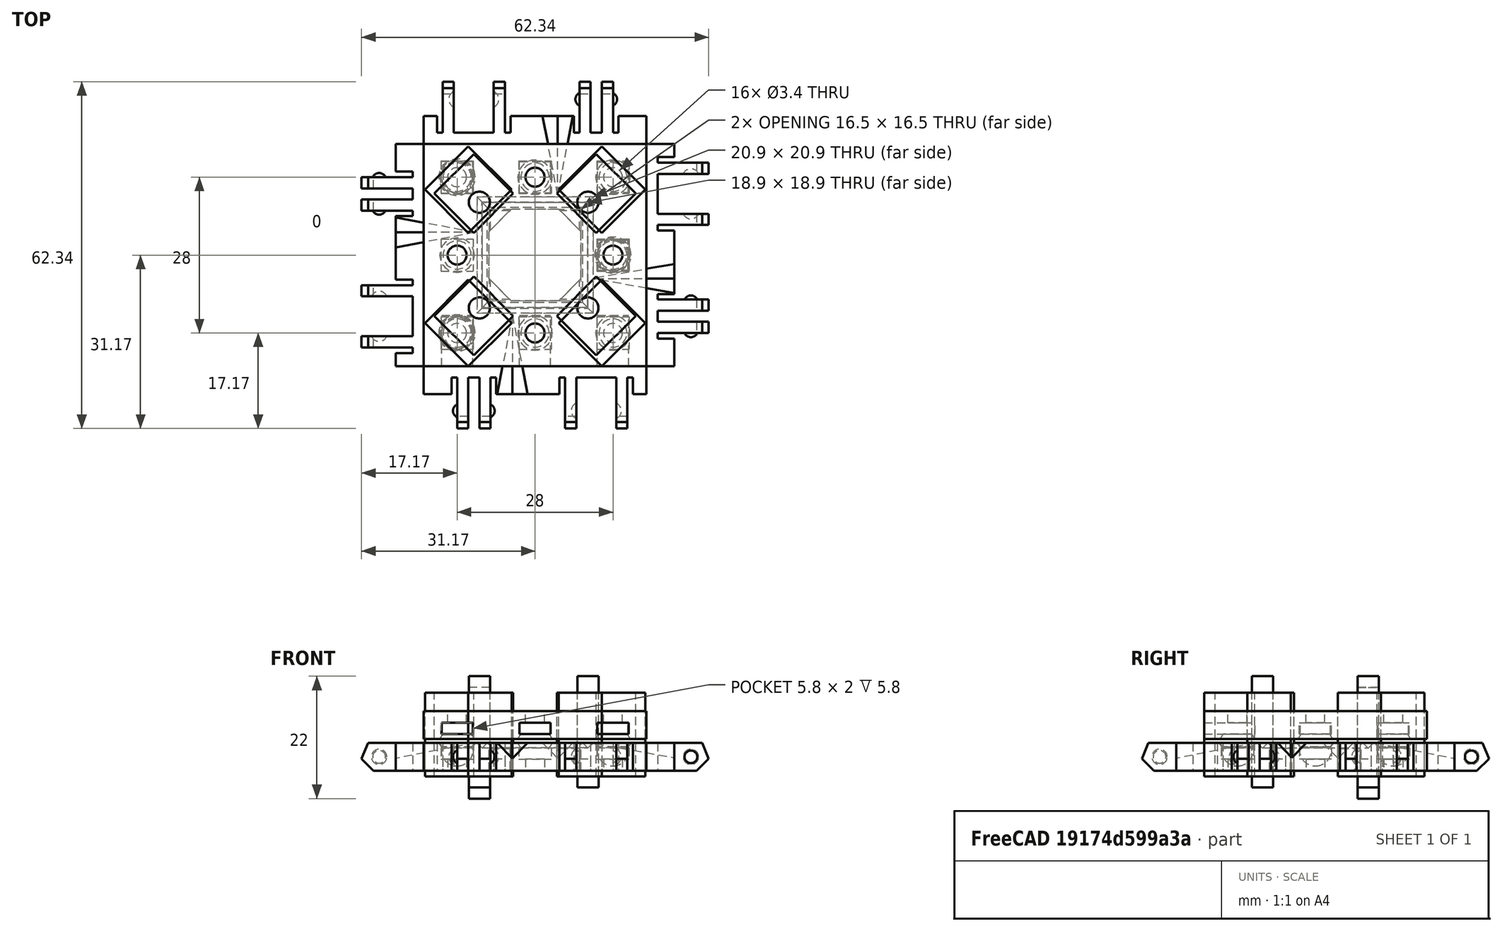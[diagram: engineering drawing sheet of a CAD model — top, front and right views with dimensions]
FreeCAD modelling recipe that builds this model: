
FCSTD DOCUMENT  (FreeCAD 0.17R13522 (Git))
Label: Robot Plates 0.1
License: All rights reserved
LicenseURL: http://en.wikipedia.org/wiki/All_rights_reserved
objects: Part::Box×147, Part::Sphere×51, Part::MultiFuse×48, Part::Cut×47, Part::Cylinder×24, Part::Chamfer×13, Part::Fuse×2, App::DocumentObjectGroup×1
note: 332 computed .brp shape members not serialized (recipe doc carries the construction recipe); baked Part::Feature solids carry a one-line shape summary decoded from their .brp

FEATURE [Part::Box] Box  label="Cube"
  AttacherType = Attacher::AttachEngine3D
  Height = 5
  Length = 40
  Placement = pos=(0,0,-2) rot=(0,0,1;0rad)
  Width = 40
FEATURE [Part::Sphere] Sphere003  label="Mag Hole 3"
  Angle1 = -90
  Angle2 = 90
  Angle3 = 360
  AttacherType = Attacher::AttachEngine3D
  Placement = pos=(6,34,1.7) rot=(0,0,1;0rad)
  Radius = 2.85
FEATURE [Part::Sphere] Sphere005  label="Mag Hole 2"
  Angle1 = -90
  Angle2 = 90
  Angle3 = 360
  AttacherType = Attacher::AttachEngine3D
  Placement = pos=(34,20,1.7) rot=(0,0,1;0rad)
  Radius = 2.85
FEATURE [Part::Sphere] Sphere  label="Mag Hole"
  Angle1 = -90
  Angle2 = 90
  Angle3 = 360
  AttacherType = Attacher::AttachEngine3D
  Placement = pos=(6,6,1.7) rot=(0,0,1;0rad)
  Radius = 2.85
FEATURE [Part::MultiFuse] Fusion004
  Shapes = -> [Sphere,Sphere005,Sphere003]
FEATURE [Part::Cut] Cut003
  Base = -> Box
  Tool = -> Fusion004
FEATURE [Part::Chamfer] Chamfer
  Base = -> Cut003
  Edges = 3 edges r=0.75: [Edge10,Edge11,Edge12]
FEATURE [Part::Box] Box001  label="Cube001"
  AttacherType = Attacher::AttachEngine3D
  Height = 7
  Length = 5
  Width = 40
FEATURE [Part::Box] Box002  label="Cube002"
  AttacherType = Attacher::AttachEngine3D
  Height = 7
  Length = 10
  Placement = pos=(-10,6,0) rot=(0,0,1;0rad)
  Width = 2
FEATURE [Part::Box] Box003  label="Cube003"
  AttacherType = Attacher::AttachEngine3D
  Height = 7
  Length = 10
  Placement = pos=(-10,10,0) rot=(0,0,1;0rad)
  Width = 2
FEATURE [Part::Box] Box004  label="Cube004"
  AttacherType = Attacher::AttachEngine3D
  Height = 7
  Length = 10
  Placement = pos=(-10,25.4,0) rot=(0,0,1;0rad)
  Width = 2
FEATURE [Part::Box] Box005  label="Cube005"
  AttacherType = Attacher::AttachEngine3D
  Height = 7
  Length = 10
  Placement = pos=(-10,34.6,0) rot=(0,0,1;0rad)
  Width = 2
FEATURE [Part::Sphere] Sphere008
  Angle1 = -90
  Angle2 = 90
  Angle3 = 360
  AttacherType = Attacher::AttachEngine3D
  Placement = pos=(-3,6.5,2.5) rot=(0,0,1;0rad)
  Radius = 1.25
FEATURE [Part::Box] Box006  label="Cube006"
  AttacherType = Attacher::AttachEngine3D
  Height = 10
  Length = 13
  Placement = pos=(-10.19,0,-1.19) rot=(0,-1,0;0.785398rad)
  Width = 40
FEATURE [Part::Sphere] Sphere009
  Angle1 = -90
  Angle2 = 90
  Angle3 = 360
  AttacherType = Attacher::AttachEngine3D
  Placement = pos=(-3,11.5,2.5) rot=(0,0,1;0rad)
  Radius = 1.25
FEATURE [Part::Sphere] Sphere010
  Angle1 = -90
  Angle2 = 90
  Angle3 = 360
  AttacherType = Attacher::AttachEngine3D
  Placement = pos=(-3,28,2.5) rot=(0,0,1;0rad)
  Radius = 1.5
FEATURE [Part::Sphere] Sphere011
  Angle1 = -90
  Angle2 = 90
  Angle3 = 360
  AttacherType = Attacher::AttachEngine3D
  Placement = pos=(-3,34,2.5) rot=(0,0,1;0rad)
  Radius = 1.5
FEATURE [Part::MultiFuse] Fusion
  Shapes = -> [Box001,Box002,Box003,Box004,Box005]
FEATURE [Part::Cut] Cut
  Base = -> Fusion
  Tool = -> Box006
FEATURE [Part::MultiFuse] Fusion001
  Shapes = -> [Sphere008,Sphere009,Cut]
FEATURE [Part::MultiFuse] Fusion002
  Shapes = -> [Sphere011,Sphere010]
FEATURE [Part::Cut] Cut001
  Base = -> Fusion001
  Tool = -> Fusion002
FEATURE [Part::Chamfer] Chamfer001
  Base = -> Cut001
  Edges = 4 edges r=4: [Edge31,Edge37,Edge43,Edge46]
FEATURE [Part::Box] Box007  label="Cube007"
  AttacherType = Attacher::AttachEngine3D
  Height = 7
  Length = 4
  Placement = pos=(-1,5,0) rot=(0,0,1;0rad)
  Width = 1
FEATURE [Part::Box] Box008  label="Cube008"
  AttacherType = Attacher::AttachEngine3D
  Height = 7
  Length = 4
  Placement = pos=(-1,8,0) rot=(0,0,1;0rad)
  Width = 2
FEATURE [Part::Box] Box009  label="Cube009"
  AttacherType = Attacher::AttachEngine3D
  Height = 7
  Length = 4
  Placement = pos=(-1,12,0) rot=(0,0,1;0rad)
  Width = 1
FEATURE [Part::Box] Box010  label="Cube010"
  AttacherType = Attacher::AttachEngine3D
  Height = 7
  Length = 4
  Placement = pos=(-1,24.4,0) rot=(0,0,1;0rad)
  Width = 1
FEATURE [Part::Box] Box011  label="Cube011"
  AttacherType = Attacher::AttachEngine3D
  Height = 7
  Length = 4
  Placement = pos=(-1,36.6,0) rot=(0,0,1;0rad)
  Width = 1
FEATURE [Part::Box] Box012  label="Cube012"
  AttacherType = Attacher::AttachEngine3D
  Height = 7
  Length = 4
  Placement = pos=(-1,27.4,0) rot=(0,0,1;0rad)
  Width = 7.2
FEATURE [Part::MultiFuse] Fusion003
  Shapes = -> [Box012,Box009,Box011,Box008,Box010,Box007]
FEATURE [Part::Cut] Cut002
  Base = -> Chamfer001
  Placement = pos=(-5,40,3) rot=(1,0,0;3.14159rad)
  Tool = -> Fusion003
FEATURE [Part::Box] Box013  label="Cube013"
  AttacherType = Attacher::AttachEngine3D
  Height = 10
  Length = 12
  Placement = pos=(-11,-2,-12) rot=(0,0,1;0rad)
  Width = 44
FEATURE [Part::Cut] Cut004
  Base = -> Cut002
  Tool = -> Box013
FEATURE [Part::Box] Box014  label="Cube014"
  AttacherType = Attacher::AttachEngine3D
  Height = 7
  Length = 10
  Placement = pos=(-10,34.6,0) rot=(0,0,1;0rad)
  Width = 2
FEATURE [Part::Box] Box015  label="Cube015"
  AttacherType = Attacher::AttachEngine3D
  Height = 7
  Length = 5
  Width = 40
FEATURE [Part::Box] Box016  label="Cube016"
  AttacherType = Attacher::AttachEngine3D
  Height = 7
  Length = 10
  Placement = pos=(-10,25.4,0) rot=(0,0,1;0rad)
  Width = 2
FEATURE [Part::Box] Box017  label="Cube017"
  AttacherType = Attacher::AttachEngine3D
  Height = 7
  Length = 10
  Placement = pos=(-10,10,0) rot=(0,0,1;0rad)
  Width = 2
FEATURE [Part::Box] Box018  label="Cube018"
  AttacherType = Attacher::AttachEngine3D
  Height = 7
  Length = 10
  Placement = pos=(-10,6,0) rot=(0,0,1;0rad)
  Width = 2
FEATURE [Part::Sphere] Sphere012
  Angle1 = -90
  Angle2 = 90
  Angle3 = 360
  AttacherType = Attacher::AttachEngine3D
  Placement = pos=(-3,6.5,2.5) rot=(0,0,1;0rad)
  Radius = 1.25
FEATURE [Part::Box] Box019  label="Cube019"
  AttacherType = Attacher::AttachEngine3D
  Height = 10
  Length = 13
  Placement = pos=(-10.19,0,-1.19) rot=(0,-1,0;0.785398rad)
  Width = 40
FEATURE [Part::Sphere] Sphere013
  Angle1 = -90
  Angle2 = 90
  Angle3 = 360
  AttacherType = Attacher::AttachEngine3D
  Placement = pos=(-3,11.5,2.5) rot=(0,0,1;0rad)
  Radius = 1.25
FEATURE [Part::Sphere] Sphere014
  Angle1 = -90
  Angle2 = 90
  Angle3 = 360
  AttacherType = Attacher::AttachEngine3D
  Placement = pos=(-3,28,2.5) rot=(0,0,1;0rad)
  Radius = 1.5
FEATURE [Part::Sphere] Sphere015
  Angle1 = -90
  Angle2 = 90
  Angle3 = 360
  AttacherType = Attacher::AttachEngine3D
  Placement = pos=(-3,34,2.5) rot=(0,0,1;0rad)
  Radius = 1.5
FEATURE [Part::MultiFuse] Fusion005
  Shapes = -> [Box015,Box018,Box017,Box016,Box014]
FEATURE [Part::Cut] Cut005
  Base = -> Fusion005
  Tool = -> Box019
FEATURE [Part::MultiFuse] Fusion006
  Shapes = -> [Sphere012,Sphere013,Cut005]
FEATURE [Part::MultiFuse] Fusion007
  Shapes = -> [Sphere015,Sphere014]
FEATURE [Part::Cut] Cut006
  Base = -> Fusion006
  Tool = -> Fusion007
FEATURE [Part::Chamfer] Chamfer002
  Base = -> Cut006
  Edges = 4 edges r=4: [Edge31,Edge37,Edge43,Edge46]
FEATURE [Part::Box] Box020  label="Cube020"
  AttacherType = Attacher::AttachEngine3D
  Height = 7
  Length = 4
  Placement = pos=(-1,5,0) rot=(0,0,1;0rad)
  Width = 1
FEATURE [Part::Box] Box021  label="Cube021"
  AttacherType = Attacher::AttachEngine3D
  Height = 7
  Length = 4
  Placement = pos=(-1,8,0) rot=(0,0,1;0rad)
  Width = 2
FEATURE [Part::Box] Box022  label="Cube022"
  AttacherType = Attacher::AttachEngine3D
  Height = 7
  Length = 4
  Placement = pos=(-1,12,0) rot=(0,0,1;0rad)
  Width = 1
FEATURE [Part::Box] Box023  label="Cube023"
  AttacherType = Attacher::AttachEngine3D
  Height = 7
  Length = 4
  Placement = pos=(-1,24.4,0) rot=(0,0,1;0rad)
  Width = 1
FEATURE [Part::Box] Box024  label="Cube024"
  AttacherType = Attacher::AttachEngine3D
  Height = 7
  Length = 4
  Placement = pos=(-1,36.6,0) rot=(0,0,1;0rad)
  Width = 1
FEATURE [Part::Box] Box025  label="Cube025"
  AttacherType = Attacher::AttachEngine3D
  Height = 7
  Length = 4
  Placement = pos=(-1,27.4,0) rot=(0,0,1;0rad)
  Width = 7.2
FEATURE [Part::MultiFuse] Fusion008
  Shapes = -> [Box025,Box022,Box024,Box021,Box023,Box020]
FEATURE [Part::Cut] Cut007
  Base = -> Chamfer002
  Placement = pos=(-5,40,3) rot=(1,0,0;3.14159rad)
  Tool = -> Fusion008
FEATURE [Part::Box] Box026  label="Cube026"
  AttacherType = Attacher::AttachEngine3D
  Height = 10
  Length = 12
  Placement = pos=(-11,-2,-12) rot=(0,0,1;0rad)
  Width = 44
FEATURE [Part::Cut] Cut008
  Base = -> Cut007
  Placement = pos=(40,0,0) rot=(0,0,1;1.5708rad)
  Tool = -> Box026
FEATURE [Part::Box] Box027  label="Cube027"
  AttacherType = Attacher::AttachEngine3D
  Height = 7
  Length = 4
  Placement = pos=(-1,12,0) rot=(0,0,1;0rad)
  Width = 1
FEATURE [Part::Box] Box028  label="Cube028"
  AttacherType = Attacher::AttachEngine3D
  Height = 10
  Length = 13
  Placement = pos=(-10.19,0,-1.19) rot=(0,-1,0;0.785398rad)
  Width = 40
FEATURE [Part::Box] Box029  label="Cube029"
  AttacherType = Attacher::AttachEngine3D
  Height = 7
  Length = 4
  Placement = pos=(-1,27.4,0) rot=(0,0,1;0rad)
  Width = 7.2
FEATURE [Part::Box] Box030  label="Cube030"
  AttacherType = Attacher::AttachEngine3D
  Height = 7
  Length = 4
  Placement = pos=(-1,5,0) rot=(0,0,1;0rad)
  Width = 1
FEATURE [Part::Box] Box031  label="Cube031"
  AttacherType = Attacher::AttachEngine3D
  Height = 7
  Length = 10
  Placement = pos=(-10,6,0) rot=(0,0,1;0rad)
  Width = 2
FEATURE [Part::Box] Box032  label="Cube032"
  AttacherType = Attacher::AttachEngine3D
  Height = 10
  Length = 12
  Placement = pos=(-11,-2,-12) rot=(0,0,1;0rad)
  Width = 44
FEATURE [Part::Sphere] Sphere016
  Angle1 = -90
  Angle2 = 90
  Angle3 = 360
  AttacherType = Attacher::AttachEngine3D
  Placement = pos=(-3,6.5,2.5) rot=(0,0,1;0rad)
  Radius = 1.25
FEATURE [Part::Box] Box033  label="Cube033"
  AttacherType = Attacher::AttachEngine3D
  Height = 7
  Length = 10
  Placement = pos=(-10,25.4,0) rot=(0,0,1;0rad)
  Width = 2
FEATURE [Part::Box] Box034  label="Cube034"
  AttacherType = Attacher::AttachEngine3D
  Height = 7
  Length = 10
  Placement = pos=(-10,10,0) rot=(0,0,1;0rad)
  Width = 2
FEATURE [Part::Sphere] Sphere017
  Angle1 = -90
  Angle2 = 90
  Angle3 = 360
  AttacherType = Attacher::AttachEngine3D
  Placement = pos=(-3,28,2.5) rot=(0,0,1;0rad)
  Radius = 1.5
FEATURE [Part::Sphere] Sphere018
  Angle1 = -90
  Angle2 = 90
  Angle3 = 360
  AttacherType = Attacher::AttachEngine3D
  Placement = pos=(-3,11.5,2.5) rot=(0,0,1;0rad)
  Radius = 1.25
FEATURE [Part::Box] Box035  label="Cube035"
  AttacherType = Attacher::AttachEngine3D
  Height = 7
  Length = 4
  Placement = pos=(-1,36.6,0) rot=(0,0,1;0rad)
  Width = 1
FEATURE [Part::Sphere] Sphere019
  Angle1 = -90
  Angle2 = 90
  Angle3 = 360
  AttacherType = Attacher::AttachEngine3D
  Placement = pos=(-3,34,2.5) rot=(0,0,1;0rad)
  Radius = 1.5
FEATURE [Part::MultiFuse] Fusion011
  Shapes = -> [Sphere019,Sphere017]
FEATURE [Part::Box] Box036  label="Cube036"
  AttacherType = Attacher::AttachEngine3D
  Height = 7
  Length = 4
  Placement = pos=(-1,8,0) rot=(0,0,1;0rad)
  Width = 2
FEATURE [Part::Box] Box037  label="Cube037"
  AttacherType = Attacher::AttachEngine3D
  Height = 7
  Length = 10
  Placement = pos=(-10,34.6,0) rot=(0,0,1;0rad)
  Width = 2
FEATURE [Part::Box] Box038  label="Cube038"
  AttacherType = Attacher::AttachEngine3D
  Height = 7
  Length = 4
  Placement = pos=(-1,24.4,0) rot=(0,0,1;0rad)
  Width = 1
FEATURE [Part::MultiFuse] Fusion009
  Shapes = -> [Box029,Box027,Box035,Box036,Box038,Box030]
FEATURE [Part::Box] Box039  label="Cube039"
  AttacherType = Attacher::AttachEngine3D
  Height = 7
  Length = 5
  Width = 40
FEATURE [Part::MultiFuse] Fusion012
  Shapes = -> [Box039,Box031,Box034,Box033,Box037]
FEATURE [Part::Cut] Cut011
  Base = -> Fusion012
  Tool = -> Box028
FEATURE [Part::MultiFuse] Fusion010
  Shapes = -> [Sphere016,Sphere018,Cut011]
FEATURE [Part::Cut] Cut012
  Base = -> Fusion010
  Tool = -> Fusion011
FEATURE [Part::Chamfer] Chamfer003
  Base = -> Cut012
  Edges = 4 edges r=4: [Edge31,Edge37,Edge43,Edge46]
FEATURE [Part::Cut] Cut010
  Base = -> Chamfer003
  Placement = pos=(-5,40,3) rot=(1,0,0;3.14159rad)
  Tool = -> Fusion009
FEATURE [Part::Cut] Cut009
  Base = -> Cut010
  Placement = pos=(40,40,0) rot=(0,0,1;3.14159rad)
  Tool = -> Box032
FEATURE [Part::Sphere] Sphere020
  Angle1 = -90
  Angle2 = 90
  Angle3 = 360
  AttacherType = Attacher::AttachEngine3D
  Placement = pos=(-3,11.5,2.5) rot=(0,0,1;0rad)
  Radius = 1.25
FEATURE [Part::Box] Box040  label="Cube040"
  AttacherType = Attacher::AttachEngine3D
  Height = 7
  Length = 10
  Placement = pos=(-10,6,0) rot=(0,0,1;0rad)
  Width = 2
FEATURE [Part::Box] Box041  label="Cube041"
  AttacherType = Attacher::AttachEngine3D
  Height = 7
  Length = 4
  Placement = pos=(-1,8,0) rot=(0,0,1;0rad)
  Width = 2
FEATURE [Part::Box] Box042  label="Cube042"
  AttacherType = Attacher::AttachEngine3D
  Height = 7
  Length = 10
  Placement = pos=(-10,10,0) rot=(0,0,1;0rad)
  Width = 2
FEATURE [Part::Box] Box043  label="Cube043"
  AttacherType = Attacher::AttachEngine3D
  Height = 10
  Length = 12
  Placement = pos=(-11,-2,-12) rot=(0,0,1;0rad)
  Width = 44
FEATURE [Part::Box] Box044  label="Cube044"
  AttacherType = Attacher::AttachEngine3D
  Height = 7
  Length = 4
  Placement = pos=(-1,5,0) rot=(0,0,1;0rad)
  Width = 1
FEATURE [Part::Sphere] Sphere021
  Angle1 = -90
  Angle2 = 90
  Angle3 = 360
  AttacherType = Attacher::AttachEngine3D
  Placement = pos=(-3,28,2.5) rot=(0,0,1;0rad)
  Radius = 1.5
FEATURE [Part::Sphere] Sphere022
  Angle1 = -90
  Angle2 = 90
  Angle3 = 360
  AttacherType = Attacher::AttachEngine3D
  Placement = pos=(-3,6.5,2.5) rot=(0,0,1;0rad)
  Radius = 1.25
FEATURE [Part::Sphere] Sphere023
  Angle1 = -90
  Angle2 = 90
  Angle3 = 360
  AttacherType = Attacher::AttachEngine3D
  Placement = pos=(-3,34,2.5) rot=(0,0,1;0rad)
  Radius = 1.5
FEATURE [Part::Box] Box045  label="Cube045"
  AttacherType = Attacher::AttachEngine3D
  Height = 7
  Length = 4
  Placement = pos=(-1,12,0) rot=(0,0,1;0rad)
  Width = 1
FEATURE [Part::Box] Box046  label="Cube046"
  AttacherType = Attacher::AttachEngine3D
  Height = 7
  Length = 5
  Width = 40
FEATURE [Part::Box] Box047  label="Cube047"
  AttacherType = Attacher::AttachEngine3D
  Height = 7
  Length = 4
  Placement = pos=(-1,36.6,0) rot=(0,0,1;0rad)
  Width = 1
FEATURE [Part::Box] Box048  label="Cube048"
  AttacherType = Attacher::AttachEngine3D
  Height = 7
  Length = 4
  Placement = pos=(-1,24.4,0) rot=(0,0,1;0rad)
  Width = 1
FEATURE [Part::Box] Box049  label="Cube049"
  AttacherType = Attacher::AttachEngine3D
  Height = 7
  Length = 10
  Placement = pos=(-10,25.4,0) rot=(0,0,1;0rad)
  Width = 2
FEATURE [Part::Box] Box050  label="Cube050"
  AttacherType = Attacher::AttachEngine3D
  Height = 10
  Length = 13
  Placement = pos=(-10.19,0,-1.19) rot=(0,-1,0;0.785398rad)
  Width = 40
FEATURE [Part::Box] Box051  label="Cube051"
  AttacherType = Attacher::AttachEngine3D
  Height = 7
  Length = 10
  Placement = pos=(-10,34.6,0) rot=(0,0,1;0rad)
  Width = 2
FEATURE [Part::MultiFuse] Fusion015
  Shapes = -> [Box046,Box040,Box042,Box049,Box051]
FEATURE [Part::Cut] Cut013
  Base = -> Fusion015
  Tool = -> Box050
FEATURE [Part::MultiFuse] Fusion013
  Shapes = -> [Sphere022,Sphere020,Cut013]
FEATURE [Part::MultiFuse] Fusion016
  Shapes = -> [Sphere023,Sphere021]
FEATURE [Part::Cut] Cut014
  Base = -> Fusion013
  Tool = -> Fusion016
FEATURE [Part::Chamfer] Chamfer004
  Base = -> Cut014
  Edges = 4 edges r=4: [Edge31,Edge37,Edge43,Edge46]
FEATURE [Part::Box] Box052  label="Cube052"
  AttacherType = Attacher::AttachEngine3D
  Height = 7
  Length = 4
  Placement = pos=(-1,27.4,0) rot=(0,0,1;0rad)
  Width = 7.2
FEATURE [Part::MultiFuse] Fusion014
  Shapes = -> [Box052,Box045,Box047,Box041,Box048,Box044]
FEATURE [Part::Cut] Cut016
  Base = -> Chamfer004
  Placement = pos=(-5,40,3) rot=(1,0,0;3.14159rad)
  Tool = -> Fusion014
FEATURE [Part::Cut] Cut015
  Base = -> Cut016
  Placement = pos=(0,40,0) rot=(0,0,-1;1.5708rad)
  Tool = -> Box043
FEATURE [Part::Box] Box054  label="Cube054"
  AttacherType = Attacher::AttachEngine3D
  Height = 15
  Length = 10
  Placement = pos=(9,2,-3) rot=(0,0,1;0.785398rad)
  Width = 10
FEATURE [Part::Box] Box055  label="Cube055"
  AttacherType = Attacher::AttachEngine3D
  Height = 15
  Length = 10
  Placement = pos=(31,24,-3) rot=(0,0,1;0.785398rad)
  Width = 10
FEATURE [Part::Box] Box056  label="Cube056"
  AttacherType = Attacher::AttachEngine3D
  Height = 15
  Length = 10
  Placement = pos=(31,2,-3) rot=(0,0,1;0.785398rad)
  Width = 10
FEATURE [Part::Box] Box057  label="Cube057"
  AttacherType = Attacher::AttachEngine3D
  Height = 15
  Length = 10
  Placement = pos=(9,24,-3) rot=(0,0,1;0.785398rad)
  Width = 10
FEATURE [Part::MultiFuse] Fusion017
  Shapes = -> [Box054,Box057,Box056,Box055]
FEATURE [Part::Box] Box058  label="Cube058"
  AttacherType = Attacher::AttachEngine3D
  Height = 5
  Length = 40
  Placement = pos=(0,0,3.7) rot=(0,0,1;0rad)
  Width = 40
FEATURE [Part::Box] Box059  label="Square Nut Hole 008"
  AttacherType = Attacher::AttachEngine3D
  Height = 2
  Length = 5.6
  Placement = pos=(17.2,31.2,4.6) rot=(0,0,1;0rad)
  Width = 5.6
FEATURE [Part::Box] Box060  label="Square Nut Hole 009"
  AttacherType = Attacher::AttachEngine3D
  Height = 2
  Length = 5.6
  Placement = pos=(17.2,-0.85,4.6) rot=(0,0,1;0rad)
  Width = 10
FEATURE [Part::Box] Box061  label="Square Nut Hole 010"
  AttacherType = Attacher::AttachEngine3D
  Height = 2
  Length = 5.6
  Placement = pos=(31.2,-0.85,4.6) rot=(0,0,1;0rad)
  Width = 10
FEATURE [Part::Box] Box062  label="Square Nut Hole 011"
  AttacherType = Attacher::AttachEngine3D
  Height = 2
  Length = 5.4
  Placement = pos=(31.3,17.3,4.6) rot=(0,0,1;0rad)
  Width = 5.4
FEATURE [Part::Box] Box063  label="Square Nut Hole 012"
  AttacherType = Attacher::AttachEngine3D
  Height = 2
  Length = 5.7
  Placement = pos=(3.15,31.15,4.6) rot=(0,0,1;0rad)
  Width = 5.7
FEATURE [Part::Box] Box064  label="Square Nut Hole 013"
  AttacherType = Attacher::AttachEngine3D
  Height = 2
  Length = 5.5
  Placement = pos=(31.25,31.25,4.6) rot=(0,0,1;0rad)
  Width = 5.5
FEATURE [Part::Box] Box065  label="Square Nut Hole 014"
  AttacherType = Attacher::AttachEngine3D
  Height = 2
  Length = 5.8
  Placement = pos=(3.1,17.1,4.6) rot=(0,0,1;0rad)
  Width = 5.8
FEATURE [Part::Box] Box066  label="Square Nut Hole 015"
  AttacherType = Attacher::AttachEngine3D
  Height = 2
  Length = 5.6
  Placement = pos=(3.2,-0.85,4.6) rot=(0,0,1;0rad)
  Width = 10
FEATURE [Part::Sphere] Sphere006  label="Nut Clearence1"
  Angle1 = -90
  Angle2 = 90
  Angle3 = 360
  AttacherType = Attacher::AttachEngine3D
  Placement = pos=(6,6,2.4) rot=(0,0,1;0rad)
  Radius = 3.35
FEATURE [Part::Sphere] Sphere024
  Angle1 = -90
  Angle2 = 90
  Angle3 = 360
  AttacherType = Attacher::AttachEngine3D
  Placement = pos=(6,34,2.4) rot=(0,0,1;0rad)
  Radius = 3.35
FEATURE [Part::Sphere] Sphere007
  Angle1 = -90
  Angle2 = 90
  Angle3 = 360
  AttacherType = Attacher::AttachEngine3D
  Placement = pos=(34,20,2.4) rot=(0,0,1;0rad)
  Radius = 3.35
FEATURE [Part::Sphere] Sphere001
  Angle1 = -90
  Angle2 = 90
  Angle3 = 360
  AttacherType = Attacher::AttachEngine3D
  Placement = pos=(34,6,2.4) rot=(0,0,1;0rad)
  Radius = 3.35
FEATURE [Part::Sphere] Sphere025
  Angle1 = -90
  Angle2 = 90
  Angle3 = 360
  AttacherType = Attacher::AttachEngine3D
  Placement = pos=(20,6,2.4) rot=(0,0,1;0rad)
  Radius = 3.35
FEATURE [Part::Sphere] Sphere026
  Angle1 = -90
  Angle2 = 90
  Angle3 = 360
  AttacherType = Attacher::AttachEngine3D
  Placement = pos=(20,34,2.4) rot=(0,0,1;0rad)
  Radius = 3.35
FEATURE [Part::Sphere] Sphere004
  Angle1 = -90
  Angle2 = 90
  Angle3 = 360
  AttacherType = Attacher::AttachEngine3D
  Placement = pos=(6,20,2.4) rot=(0,0,1;0rad)
  Radius = 3.35
FEATURE [Part::Sphere] Sphere002
  Angle1 = -90
  Angle2 = 90
  Angle3 = 360
  AttacherType = Attacher::AttachEngine3D
  Placement = pos=(34,34,2.4) rot=(0,0,1;0rad)
  Radius = 3.35
FEATURE [Part::Cylinder] Cylinder
  Angle = 360
  AttacherType = Attacher::AttachEngine3D
  Height = 10
  Placement = pos=(6,6,0) rot=(0,0,1;0rad)
  Radius = 1.7
FEATURE [Part::Cylinder] Cylinder002
  Angle = 360
  AttacherType = Attacher::AttachEngine3D
  Height = 10
  Placement = pos=(34,6,0) rot=(0,0,1;0rad)
  Radius = 1.7
FEATURE [Part::Cylinder] Cylinder001
  Angle = 360
  AttacherType = Attacher::AttachEngine3D
  Height = 10
  Placement = pos=(20,6,0) rot=(0,0,1;0rad)
  Radius = 1.7
FEATURE [Part::Cylinder] Cylinder003
  Angle = 360
  AttacherType = Attacher::AttachEngine3D
  Height = 10
  Placement = pos=(34,34,0) rot=(0,0,1;0rad)
  Radius = 1.7
FEATURE [Part::Cylinder] Cylinder004
  Angle = 360
  AttacherType = Attacher::AttachEngine3D
  Height = 10
  Placement = pos=(20,34,0) rot=(0,0,1;0rad)
  Radius = 1.7
FEATURE [Part::Cylinder] Cylinder005
  Angle = 360
  AttacherType = Attacher::AttachEngine3D
  Height = 10
  Placement = pos=(6,34,0) rot=(0,0,1;0rad)
  Radius = 1.7
FEATURE [Part::Cylinder] Cylinder006
  Angle = 360
  AttacherType = Attacher::AttachEngine3D
  Height = 10
  Placement = pos=(6,20,0) rot=(0,0,1;0rad)
  Radius = 1.7
FEATURE [Part::Cylinder] Cylinder007
  Angle = 360
  AttacherType = Attacher::AttachEngine3D
  Height = 10
  Placement = pos=(34,20,0) rot=(0,0,1;0rad)
  Radius = 1.7
FEATURE [Part::MultiFuse] Fusion018
  Shapes = -> [Cylinder,Cylinder004,Cylinder007,Cylinder005,Cylinder006,Cylinder001,Cylinder002,Cylinder003]
FEATURE [Part::MultiFuse] Fusion019
  Shapes = -> [Sphere007,Sphere024,Sphere006,Sphere025,Sphere001,Sphere026,Sphere004,Sphere002]
FEATURE [Part::MultiFuse] Fusion020
  Shapes = -> [Box061,Box065,Box062,Box063,Box064,Box066,Box059,Box060]
FEATURE [Part::Cut] Cut017
  Base = -> Box058
  Tool = -> Fusion020
FEATURE [Part::Cut] Cut019
  Base = -> Cut017
  Tool = -> Fusion019
FEATURE [Part::Cut] Cut018
  Base = -> Cut019
  Tool = -> Fusion018
FEATURE [Part::Cylinder] Cylinder008
  Angle = 360
  AttacherType = Attacher::AttachEngine3D
  Height = 20
  Placement = pos=(10,10.5,-5) rot=(0,0,1;0rad)
  Radius = 1.9
FEATURE [Part::Cylinder] Cylinder009
  Angle = 360
  AttacherType = Attacher::AttachEngine3D
  Height = 20
  Placement = pos=(29.5,10.5,-5) rot=(0,0,1;0rad)
  Radius = 1.9
FEATURE [Part::Cylinder] Cylinder010
  Angle = 360
  AttacherType = Attacher::AttachEngine3D
  Height = 20
  Placement = pos=(29.5,29.5,-5) rot=(0,0,1;0rad)
  Radius = 1.9
FEATURE [Part::Cylinder] Cylinder011
  Angle = 360
  AttacherType = Attacher::AttachEngine3D
  Height = 20
  Placement = pos=(10,29.5,-7) rot=(0,0,1;0rad)
  Radius = 1.9
FEATURE [Part::MultiFuse] Fusion021  label="M2 Screw holes"
  Shapes = -> [Cylinder008,Cylinder009,Cylinder011,Cylinder010]
FEATURE [Part::Box] Box067  label="Square Nut Hole 016"
  AttacherType = Attacher::AttachEngine3D
  Height = 2
  Length = 5.8
  Placement = pos=(31.1,17.1,4.6) rot=(0,0,1;0rad)
  Width = 5.8
FEATURE [Part::Box] Box068  label="Square Nut Hole 017"
  AttacherType = Attacher::AttachEngine3D
  Height = 2
  Length = 5.8
  Placement = pos=(17.1,3.1,4.6) rot=(0,0,1;0rad)
  Width = 5.8
FEATURE [Part::Box] Box069  label="Square Nut Hole 018"
  AttacherType = Attacher::AttachEngine3D
  Height = 2
  Length = 5.8
  Placement = pos=(31.1,3.1,4.6) rot=(0,0,1;0rad)
  Width = 5.8
FEATURE [Part::Box] Box070  label="Square Nut Hole 019"
  AttacherType = Attacher::AttachEngine3D
  Height = 2
  Length = 5.8
  Placement = pos=(3.1,3.1,4.6) rot=(0,0,1;0rad)
  Width = 5.8
FEATURE [Part::Box] Box071  label="Square Nut Hole 020"
  AttacherType = Attacher::AttachEngine3D
  Height = 2
  Length = 5.8
  Placement = pos=(3.1,31.1,4.6) rot=(0,0,1;0rad)
  Width = 5.8
FEATURE [Part::Box] Box072  label="Square Nut Hole 021"
  AttacherType = Attacher::AttachEngine3D
  Height = 2
  Length = 5.8
  Placement = pos=(17.1,31.1,4.6) rot=(0,0,1;0rad)
  Width = 5.8
FEATURE [Part::Box] Box073  label="Square Nut Hole 022"
  AttacherType = Attacher::AttachEngine3D
  Height = 2
  Length = 5.8
  Placement = pos=(31.1,31.1,4.6) rot=(0,0,1;0rad)
  Width = 5.8
FEATURE [Part::Box] Box074  label="Square Nut Hole 023"
  AttacherType = Attacher::AttachEngine3D
  Height = 2
  Length = 5.8
  Placement = pos=(3.1,17.1,4.6) rot=(0,0,1;0rad)
  Width = 5.8
FEATURE [Part::Cylinder] Cylinder012
  Angle = 360
  AttacherType = Attacher::AttachEngine3D
  Height = 10
  Placement = pos=(6,6,0) rot=(0,0,1;0rad)
  Radius = 1.7
FEATURE [Part::Cylinder] Cylinder013
  Angle = 360
  AttacherType = Attacher::AttachEngine3D
  Height = 10
  Placement = pos=(34,34,0) rot=(0,0,1;0rad)
  Radius = 1.7
FEATURE [Part::Cylinder] Cylinder014
  Angle = 360
  AttacherType = Attacher::AttachEngine3D
  Height = 10
  Placement = pos=(20,34,0) rot=(0,0,1;0rad)
  Radius = 1.7
FEATURE [Part::Cylinder] Cylinder015
  Angle = 360
  AttacherType = Attacher::AttachEngine3D
  Height = 10
  Placement = pos=(6,34,0) rot=(0,0,1;0rad)
  Radius = 1.7
FEATURE [Part::Cylinder] Cylinder016
  Angle = 360
  AttacherType = Attacher::AttachEngine3D
  Height = 10
  Placement = pos=(6,20,0) rot=(0,0,1;0rad)
  Radius = 1.7
FEATURE [Part::Cylinder] Cylinder017
  Angle = 360
  AttacherType = Attacher::AttachEngine3D
  Height = 10
  Placement = pos=(34,20,0) rot=(0,0,1;0rad)
  Radius = 1.7
FEATURE [Part::Cylinder] Cylinder018
  Angle = 360
  AttacherType = Attacher::AttachEngine3D
  Height = 10
  Placement = pos=(34,6,0) rot=(0,0,1;0rad)
  Radius = 1.7
FEATURE [Part::Cylinder] Cylinder019
  Angle = 360
  AttacherType = Attacher::AttachEngine3D
  Height = 10
  Placement = pos=(20,6,0) rot=(0,0,1;0rad)
  Radius = 1.7
FEATURE [Part::Box] Box075  label="Cube059"
  AttacherType = Attacher::AttachEngine3D
  Height = 5
  Length = 40
  Placement = pos=(0,0,-2) rot=(0,0,1;0rad)
  Width = 40
FEATURE [Part::Sphere] Sphere027
  Angle1 = -90
  Angle2 = 90
  Angle3 = 360
  AttacherType = Attacher::AttachEngine3D
  Placement = pos=(34,20,2.4) rot=(0,0,1;0rad)
  Radius = 3.35
FEATURE [Part::Sphere] Sphere028  label="Nut Clearence002"
  Angle1 = -90
  Angle2 = 90
  Angle3 = 360
  AttacherType = Attacher::AttachEngine3D
  Placement = pos=(6,6,2.4) rot=(0,0,1;0rad)
  Radius = 3.35
FEATURE [Part::Sphere] Sphere029
  Angle1 = -90
  Angle2 = 90
  Angle3 = 360
  AttacherType = Attacher::AttachEngine3D
  Placement = pos=(34,34,2.4) rot=(0,0,1;0rad)
  Radius = 3.35
FEATURE [Part::Sphere] Sphere030
  Angle1 = -90
  Angle2 = 90
  Angle3 = 360
  AttacherType = Attacher::AttachEngine3D
  Placement = pos=(34,6,2.4) rot=(0,0,1;0rad)
  Radius = 3.35
FEATURE [Part::Sphere] Sphere031
  Angle1 = -90
  Angle2 = 90
  Angle3 = 360
  AttacherType = Attacher::AttachEngine3D
  Placement = pos=(20,6,2.4) rot=(0,0,1;0rad)
  Radius = 3.35
FEATURE [Part::Sphere] Sphere032
  Angle1 = -90
  Angle2 = 90
  Angle3 = 360
  AttacherType = Attacher::AttachEngine3D
  Placement = pos=(6,34,2.4) rot=(0,0,1;0rad)
  Radius = 3.35
FEATURE [Part::Sphere] Sphere033
  Angle1 = -90
  Angle2 = 90
  Angle3 = 360
  AttacherType = Attacher::AttachEngine3D
  Placement = pos=(6,20,2.4) rot=(0,0,1;0rad)
  Radius = 3.35
FEATURE [Part::Sphere] Sphere034
  Angle1 = -90
  Angle2 = 90
  Angle3 = 360
  AttacherType = Attacher::AttachEngine3D
  Placement = pos=(20,34,2.4) rot=(0,0,1;0rad)
  Radius = 3.35
FEATURE [Part::Box] Box076  label="Cube060"
  AttacherType = Attacher::AttachEngine3D
  Height = 15
  Length = 16.5
  Placement = pos=(11.75,11.75,-3) rot=(0,0,1;0rad)
  Width = 16.5
FEATURE [Part::Box] Box077  label="Cube061"
  AttacherType = Attacher::AttachEngine3D
  Height = 15
  Length = 11
  Placement = pos=(8,24,-3) rot=(0,0,1;0.785398rad)
  Width = 11
FEATURE [Part::Box] Box078  label="Cube062"
  AttacherType = Attacher::AttachEngine3D
  Height = 15
  Length = 11
  Placement = pos=(8,0,-3) rot=(0,0,1;0.785398rad)
  Width = 11
FEATURE [Part::Box] Box079  label="Cube063"
  AttacherType = Attacher::AttachEngine3D
  Height = 15
  Length = 11
  Placement = pos=(32,0,-3) rot=(0,0,1;0.785398rad)
  Width = 11
FEATURE [Part::Box] Box080  label="Cube064"
  AttacherType = Attacher::AttachEngine3D
  Height = 15
  Length = 11
  Placement = pos=(32,24,-3) rot=(0,0,1;0.785398rad)
  Width = 11
FEATURE [Part::MultiFuse] Fusion022
  Shapes = -> [Box078,Box077,Box079,Box080]
FEATURE [Part::Cylinder] Cylinder020
  Angle = 360
  AttacherType = Attacher::AttachEngine3D
  Height = 20
  Placement = pos=(29.5,10.5,-5) rot=(0,0,1;0rad)
  Radius = 1.9
FEATURE [Part::Cylinder] Cylinder021
  Angle = 360
  AttacherType = Attacher::AttachEngine3D
  Height = 20
  Placement = pos=(10,29.5,-7) rot=(0,0,1;0rad)
  Radius = 1.9
FEATURE [Part::Cylinder] Cylinder022
  Angle = 360
  AttacherType = Attacher::AttachEngine3D
  Height = 20
  Placement = pos=(10,10.5,-5) rot=(0,0,1;0rad)
  Radius = 1.9
FEATURE [Part::Cylinder] Cylinder023
  Angle = 360
  AttacherType = Attacher::AttachEngine3D
  Height = 20
  Placement = pos=(29.5,29.5,-5) rot=(0,0,1;0rad)
  Radius = 1.9
FEATURE [Part::MultiFuse] Fusion023  label="M2 Screw holes001"
  Shapes = -> [Cylinder022,Cylinder020,Cylinder021,Cylinder023]
FEATURE [Part::MultiFuse] Fusion024  label="Square Nut Hole"
  Shapes = -> [Box067,Box073,Box071,Box069,Box068,Box070,Box072,Box074]
FEATURE [Part::MultiFuse] Fusion025  label="Square Nut Screw Holes"
  Shapes = -> [Cylinder012,Cylinder018,Cylinder016,Cylinder015,Cylinder014,Cylinder013,Cylinder017,Cylinder019]
FEATURE [Part::MultiFuse] Fusion026  label="Nut Chamfers"
  Shapes = -> [Sphere027,Sphere028,Sphere029,Sphere031,Sphere032,Sphere033,Sphere034,Sphere030]
FEATURE [App::DocumentObjectGroup] Group  label="Cubes"
  Group = -> [Fusion017,Fusion022]
FEATURE [Part::Box] Box082  label="Cube066"
  AttacherType = Attacher::AttachEngine3D
  Height = 10
  Length = 15
  Placement = pos=(30.8481,15.8,2.86019) rot=(0.974848,0.205904,-0.085288;0.803573rad)
  Width = 10
FEATURE [Part::Box] Box083  label="Cube067"
  AttacherType = Attacher::AttachEngine3D
  Height = 10
  Length = 21
  Placement = pos=(9.5,9.5,2.1) rot=(0,0,1;0rad)
  Width = 21
FEATURE [Part::Box] Box084  label="Cube068"
  AttacherType = Attacher::AttachEngine3D
  Height = 14
  Length = 17
  Placement = pos=(11.5,11.5,0) rot=(0,0,1;0rad)
  Width = 17
FEATURE [Part::Cut] Cut020
  Base = -> Box083
  Tool = -> Box084
FEATURE [Part::Chamfer] Chamfer007
  Base = -> Cut020
  Edges = 8 edges r=0.95: [Edge4,Edge5,Edge14,Edge16,Edge17,Edge18,Edge19,Edge20]
FEATURE [Part::Cut] Cut021
  Base = -> Chamfer
  Tool = -> Chamfer007
FEATURE [Part::Chamfer] Chamfer008
  Base = -> Box076
  Edges = 4 edges r=4: [Edge1,Edge3,Edge5,Edge7]
FEATURE [Part::Cut] Cut022
  Base = -> Cut021
  Tool = -> Chamfer008
FEATURE [Part::Box] Box085  label="Cube069"
  AttacherType = Attacher::AttachEngine3D
  Height = 15
  Length = 16
  Placement = pos=(12,12,-13) rot=(0,0,1;0rad)
  Width = 16
FEATURE [Part::Cut] Cut023
  Base = -> Cut022
  Tool = -> Box085
FEATURE [Part::Box] Box086  label="Cube070"
  AttacherType = Attacher::AttachEngine3D
  Height = 10
  Length = 10
  Placement = pos=(17,32.0919,9.95) rot=(-0.225436,0.969773,-0.093378;0.807337rad)
  Width = 15
FEATURE [Part::Box] Box087  label="Cube071"
  AttacherType = Attacher::AttachEngine3D
  Height = 10
  Length = 10
  Placement = pos=(7.9081,17,9.95) rot=(-0.450607,0.280623,0.847469;1.65638rad)
  Width = 15
FEATURE [Part::Box] Box088  label="Cube072"
  AttacherType = Attacher::AttachEngine3D
  Height = 10
  Length = 10
  Placement = pos=(23,7.9081,9.95) rot=(-0.381178,-0.08861,0.920245;3.06822rad)
  Width = 15
FEATURE [Part::MultiFuse] Fusion027
  Shapes = -> [Box086,Box082,Box087,Box088]
FEATURE [Part::MultiFuse] Fusion028
  Shapes = -> [Cut015,Cut004,Cut008,Cut009]
FEATURE [Part::Fuse] Fusion029
  Base = -> Cut023
  Tool = -> Fusion028
FEATURE [Part::Cut] Cut024
  Base = -> Fusion029
  Tool = -> Fusion027
FEATURE [Part::Box] Box089  label="Cube073"
  AttacherType = Attacher::AttachEngine3D
  Height = 10
  Length = 10
  Placement = pos=(17,32.0919,9.95) rot=(-0.225436,0.969773,-0.093378;0.807337rad)
  Width = 15
FEATURE [Part::Box] Box090  label="Cube074"
  AttacherType = Attacher::AttachEngine3D
  Height = 10
  Length = 15
  Placement = pos=(30.8481,15.8,2.86019) rot=(0.974848,0.205904,-0.085288;0.803573rad)
  Width = 10
FEATURE [Part::Box] Box091  label="Cube075"
  AttacherType = Attacher::AttachEngine3D
  Height = 10
  Length = 10
  Placement = pos=(7.9081,17,9.95) rot=(-0.450607,0.280623,0.847469;1.65638rad)
  Width = 15
FEATURE [Part::Box] Box092  label="Cube076"
  AttacherType = Attacher::AttachEngine3D
  Height = 10
  Length = 10
  Placement = pos=(23,7.9081,9.95) rot=(-0.381178,-0.08861,0.920245;3.06822rad)
  Width = 15
FEATURE [Part::Box] Box093  label="Cube077"
  AttacherType = Attacher::AttachEngine3D
  Height = 7
  Length = 5
  Width = 40
FEATURE [Part::Box] Box094  label="Cube078"
  AttacherType = Attacher::AttachEngine3D
  Height = 7
  Length = 10
  Placement = pos=(-10,6,0) rot=(0,0,1;0rad)
  Width = 2
FEATURE [Part::Box] Box095  label="Cube079"
  AttacherType = Attacher::AttachEngine3D
  Height = 7
  Length = 10
  Placement = pos=(-10,10,0) rot=(0,0,1;0rad)
  Width = 2
FEATURE [Part::Box] Box096  label="Cube080"
  AttacherType = Attacher::AttachEngine3D
  Height = 7
  Length = 10
  Placement = pos=(-10,25.4,0) rot=(0,0,1;0rad)
  Width = 2
FEATURE [Part::Box] Box097  label="Cube081"
  AttacherType = Attacher::AttachEngine3D
  Height = 7
  Length = 10
  Placement = pos=(-10,34.6,0) rot=(0,0,1;0rad)
  Width = 2
FEATURE [Part::Sphere] Sphere035
  Angle1 = -90
  Angle2 = 90
  Angle3 = 360
  AttacherType = Attacher::AttachEngine3D
  Placement = pos=(-3,6.5,2.5) rot=(0,0,1;0rad)
  Radius = 1.25
FEATURE [Part::Box] Box098  label="Cube082"
  AttacherType = Attacher::AttachEngine3D
  Height = 10
  Length = 13
  Placement = pos=(-10.19,0,-1.19) rot=(0,-1,0;0.785398rad)
  Width = 40
FEATURE [Part::Sphere] Sphere036
  Angle1 = -90
  Angle2 = 90
  Angle3 = 360
  AttacherType = Attacher::AttachEngine3D
  Placement = pos=(-3,11.5,2.5) rot=(0,0,1;0rad)
  Radius = 1.25
FEATURE [Part::Sphere] Sphere037
  Angle1 = -90
  Angle2 = 90
  Angle3 = 360
  AttacherType = Attacher::AttachEngine3D
  Placement = pos=(-3,28,2.5) rot=(0,0,1;0rad)
  Radius = 1.5
FEATURE [Part::Sphere] Sphere038
  Angle1 = -90
  Angle2 = 90
  Angle3 = 360
  AttacherType = Attacher::AttachEngine3D
  Placement = pos=(-3,34,2.5) rot=(0,0,1;0rad)
  Radius = 1.5
FEATURE [Part::MultiFuse] Fusion030
  Shapes = -> [Box093,Box094,Box095,Box096,Box097]
FEATURE [Part::Cut] Cut025
  Base = -> Fusion030
  Tool = -> Box098
FEATURE [Part::MultiFuse] Fusion031
  Shapes = -> [Sphere035,Sphere036,Cut025]
FEATURE [Part::MultiFuse] Fusion032
  Shapes = -> [Sphere038,Sphere037]
FEATURE [Part::Cut] Cut026
  Base = -> Fusion031
  Tool = -> Fusion032
FEATURE [Part::Chamfer] Chamfer009
  Base = -> Cut026
  Edges = 4 edges r=4: [Edge31,Edge37,Edge43,Edge46]
FEATURE [Part::Box] Box099  label="Cube083"
  AttacherType = Attacher::AttachEngine3D
  Height = 7
  Length = 4
  Placement = pos=(-1,5,0) rot=(0,0,1;0rad)
  Width = 1
FEATURE [Part::Box] Box100  label="Cube084"
  AttacherType = Attacher::AttachEngine3D
  Height = 7
  Length = 4
  Placement = pos=(-1,8,0) rot=(0,0,1;0rad)
  Width = 2
FEATURE [Part::Box] Box101  label="Cube085"
  AttacherType = Attacher::AttachEngine3D
  Height = 7
  Length = 4
  Placement = pos=(-1,12,0) rot=(0,0,1;0rad)
  Width = 1
FEATURE [Part::Box] Box102  label="Cube086"
  AttacherType = Attacher::AttachEngine3D
  Height = 7
  Length = 4
  Placement = pos=(-1,24.4,0) rot=(0,0,1;0rad)
  Width = 1
FEATURE [Part::Box] Box103  label="Cube087"
  AttacherType = Attacher::AttachEngine3D
  Height = 7
  Length = 4
  Placement = pos=(-1,36.6,0) rot=(0,0,1;0rad)
  Width = 1
FEATURE [Part::Box] Box104  label="Cube088"
  AttacherType = Attacher::AttachEngine3D
  Height = 7
  Length = 4
  Placement = pos=(-1,27.4,0) rot=(0,0,1;0rad)
  Width = 7.2
FEATURE [Part::MultiFuse] Fusion033
  Shapes = -> [Box104,Box101,Box103,Box100,Box102,Box099]
FEATURE [Part::Cut] Cut027
  Base = -> Chamfer009
  Placement = pos=(-5,40,3) rot=(1,0,0;3.14159rad)
  Tool = -> Fusion033
FEATURE [Part::Box] Box105  label="Cube089"
  AttacherType = Attacher::AttachEngine3D
  Height = 10
  Length = 12
  Placement = pos=(-11,-2,-12) rot=(0,0,1;0rad)
  Width = 44
FEATURE [Part::Cut] Cut028
  Base = -> Cut027
  Tool = -> Box105
FEATURE [Part::Box] Box106  label="Cube090"
  AttacherType = Attacher::AttachEngine3D
  Height = 7
  Length = 10
  Placement = pos=(-10,34.6,0) rot=(0,0,1;0rad)
  Width = 2
FEATURE [Part::Box] Box107  label="Cube091"
  AttacherType = Attacher::AttachEngine3D
  Height = 7
  Length = 5
  Width = 40
FEATURE [Part::Box] Box108  label="Cube092"
  AttacherType = Attacher::AttachEngine3D
  Height = 7
  Length = 10
  Placement = pos=(-10,25.4,0) rot=(0,0,1;0rad)
  Width = 2
FEATURE [Part::Box] Box109  label="Cube093"
  AttacherType = Attacher::AttachEngine3D
  Height = 7
  Length = 10
  Placement = pos=(-10,10,0) rot=(0,0,1;0rad)
  Width = 2
FEATURE [Part::Box] Box110  label="Cube094"
  AttacherType = Attacher::AttachEngine3D
  Height = 7
  Length = 10
  Placement = pos=(-10,6,0) rot=(0,0,1;0rad)
  Width = 2
FEATURE [Part::Sphere] Sphere039
  Angle1 = -90
  Angle2 = 90
  Angle3 = 360
  AttacherType = Attacher::AttachEngine3D
  Placement = pos=(-3,6.5,2.5) rot=(0,0,1;0rad)
  Radius = 1.25
FEATURE [Part::Box] Box111  label="Cube095"
  AttacherType = Attacher::AttachEngine3D
  Height = 10
  Length = 13
  Placement = pos=(-10.19,0,-1.19) rot=(0,-1,0;0.785398rad)
  Width = 40
FEATURE [Part::Sphere] Sphere040
  Angle1 = -90
  Angle2 = 90
  Angle3 = 360
  AttacherType = Attacher::AttachEngine3D
  Placement = pos=(-3,11.5,2.5) rot=(0,0,1;0rad)
  Radius = 1.25
FEATURE [Part::Sphere] Sphere041
  Angle1 = -90
  Angle2 = 90
  Angle3 = 360
  AttacherType = Attacher::AttachEngine3D
  Placement = pos=(-3,28,2.5) rot=(0,0,1;0rad)
  Radius = 1.5
FEATURE [Part::Sphere] Sphere042
  Angle1 = -90
  Angle2 = 90
  Angle3 = 360
  AttacherType = Attacher::AttachEngine3D
  Placement = pos=(-3,34,2.5) rot=(0,0,1;0rad)
  Radius = 1.5
FEATURE [Part::MultiFuse] Fusion034
  Shapes = -> [Box107,Box110,Box109,Box108,Box106]
FEATURE [Part::Cut] Cut029
  Base = -> Fusion034
  Tool = -> Box111
FEATURE [Part::MultiFuse] Fusion035
  Shapes = -> [Sphere039,Sphere040,Cut029]
FEATURE [Part::MultiFuse] Fusion036
  Shapes = -> [Sphere042,Sphere041]
FEATURE [Part::Cut] Cut030
  Base = -> Fusion035
  Tool = -> Fusion036
FEATURE [Part::Chamfer] Chamfer010
  Base = -> Cut030
  Edges = 4 edges r=4: [Edge31,Edge37,Edge43,Edge46]
FEATURE [Part::Box] Box112  label="Cube096"
  AttacherType = Attacher::AttachEngine3D
  Height = 7
  Length = 4
  Placement = pos=(-1,5,0) rot=(0,0,1;0rad)
  Width = 1
FEATURE [Part::Box] Box113  label="Cube097"
  AttacherType = Attacher::AttachEngine3D
  Height = 7
  Length = 4
  Placement = pos=(-1,8,0) rot=(0,0,1;0rad)
  Width = 2
FEATURE [Part::Box] Box114  label="Cube098"
  AttacherType = Attacher::AttachEngine3D
  Height = 7
  Length = 4
  Placement = pos=(-1,12,0) rot=(0,0,1;0rad)
  Width = 1
FEATURE [Part::Box] Box115  label="Cube099"
  AttacherType = Attacher::AttachEngine3D
  Height = 7
  Length = 4
  Placement = pos=(-1,24.4,0) rot=(0,0,1;0rad)
  Width = 1
FEATURE [Part::Box] Box116  label="Cube100"
  AttacherType = Attacher::AttachEngine3D
  Height = 7
  Length = 4
  Placement = pos=(-1,36.6,0) rot=(0,0,1;0rad)
  Width = 1
FEATURE [Part::Box] Box117  label="Cube101"
  AttacherType = Attacher::AttachEngine3D
  Height = 7
  Length = 4
  Placement = pos=(-1,27.4,0) rot=(0,0,1;0rad)
  Width = 7.2
FEATURE [Part::MultiFuse] Fusion037
  Shapes = -> [Box117,Box114,Box116,Box113,Box115,Box112]
FEATURE [Part::Cut] Cut031
  Base = -> Chamfer010
  Placement = pos=(-5,40,3) rot=(1,0,0;3.14159rad)
  Tool = -> Fusion037
FEATURE [Part::Box] Box118  label="Cube102"
  AttacherType = Attacher::AttachEngine3D
  Height = 10
  Length = 12
  Placement = pos=(-11,-2,-12) rot=(0,0,1;0rad)
  Width = 44
FEATURE [Part::Cut] Cut032
  Base = -> Cut031
  Placement = pos=(40,0,0) rot=(0,0,1;1.5708rad)
  Tool = -> Box118
FEATURE [Part::Box] Box119  label="Cube103"
  AttacherType = Attacher::AttachEngine3D
  Height = 7
  Length = 4
  Placement = pos=(-1,12,0) rot=(0,0,1;0rad)
  Width = 1
FEATURE [Part::Box] Box120  label="Cube104"
  AttacherType = Attacher::AttachEngine3D
  Height = 10
  Length = 13
  Placement = pos=(-10.19,0,-1.19) rot=(0,-1,0;0.785398rad)
  Width = 40
FEATURE [Part::Box] Box121  label="Cube105"
  AttacherType = Attacher::AttachEngine3D
  Height = 7
  Length = 4
  Placement = pos=(-1,27.4,0) rot=(0,0,1;0rad)
  Width = 7.2
FEATURE [Part::Box] Box122  label="Cube106"
  AttacherType = Attacher::AttachEngine3D
  Height = 7
  Length = 4
  Placement = pos=(-1,5,0) rot=(0,0,1;0rad)
  Width = 1
FEATURE [Part::Box] Box123  label="Cube107"
  AttacherType = Attacher::AttachEngine3D
  Height = 7
  Length = 10
  Placement = pos=(-10,6,0) rot=(0,0,1;0rad)
  Width = 2
FEATURE [Part::Box] Box124  label="Cube108"
  AttacherType = Attacher::AttachEngine3D
  Height = 10
  Length = 12
  Placement = pos=(-11,-2,-12) rot=(0,0,1;0rad)
  Width = 44
FEATURE [Part::Sphere] Sphere043
  Angle1 = -90
  Angle2 = 90
  Angle3 = 360
  AttacherType = Attacher::AttachEngine3D
  Placement = pos=(-3,6.5,2.5) rot=(0,0,1;0rad)
  Radius = 1.25
FEATURE [Part::Box] Box125  label="Cube109"
  AttacherType = Attacher::AttachEngine3D
  Height = 7
  Length = 10
  Placement = pos=(-10,25.4,0) rot=(0,0,1;0rad)
  Width = 2
FEATURE [Part::Box] Box126  label="Cube110"
  AttacherType = Attacher::AttachEngine3D
  Height = 7
  Length = 10
  Placement = pos=(-10,10,0) rot=(0,0,1;0rad)
  Width = 2
FEATURE [Part::Sphere] Sphere044
  Angle1 = -90
  Angle2 = 90
  Angle3 = 360
  AttacherType = Attacher::AttachEngine3D
  Placement = pos=(-3,28,2.5) rot=(0,0,1;0rad)
  Radius = 1.5
FEATURE [Part::Sphere] Sphere045
  Angle1 = -90
  Angle2 = 90
  Angle3 = 360
  AttacherType = Attacher::AttachEngine3D
  Placement = pos=(-3,11.5,2.5) rot=(0,0,1;0rad)
  Radius = 1.25
FEATURE [Part::Box] Box127  label="Cube111"
  AttacherType = Attacher::AttachEngine3D
  Height = 7
  Length = 4
  Placement = pos=(-1,36.6,0) rot=(0,0,1;0rad)
  Width = 1
FEATURE [Part::Sphere] Sphere046
  Angle1 = -90
  Angle2 = 90
  Angle3 = 360
  AttacherType = Attacher::AttachEngine3D
  Placement = pos=(-3,34,2.5) rot=(0,0,1;0rad)
  Radius = 1.5
FEATURE [Part::MultiFuse] Fusion040
  Shapes = -> [Sphere046,Sphere044]
FEATURE [Part::Box] Box128  label="Cube112"
  AttacherType = Attacher::AttachEngine3D
  Height = 7
  Length = 4
  Placement = pos=(-1,8,0) rot=(0,0,1;0rad)
  Width = 2
FEATURE [Part::Box] Box129  label="Cube113"
  AttacherType = Attacher::AttachEngine3D
  Height = 7
  Length = 10
  Placement = pos=(-10,34.6,0) rot=(0,0,1;0rad)
  Width = 2
FEATURE [Part::Box] Box130  label="Cube114"
  AttacherType = Attacher::AttachEngine3D
  Height = 7
  Length = 4
  Placement = pos=(-1,24.4,0) rot=(0,0,1;0rad)
  Width = 1
FEATURE [Part::MultiFuse] Fusion038
  Shapes = -> [Box121,Box119,Box127,Box128,Box130,Box122]
FEATURE [Part::Box] Box131  label="Cube115"
  AttacherType = Attacher::AttachEngine3D
  Height = 7
  Length = 5
  Width = 40
FEATURE [Part::MultiFuse] Fusion041
  Shapes = -> [Box131,Box123,Box126,Box125,Box129]
FEATURE [Part::Cut] Cut035
  Base = -> Fusion041
  Tool = -> Box120
FEATURE [Part::MultiFuse] Fusion039
  Shapes = -> [Sphere043,Sphere045,Cut035]
FEATURE [Part::Cut] Cut036
  Base = -> Fusion039
  Tool = -> Fusion040
FEATURE [Part::Chamfer] Chamfer011
  Base = -> Cut036
  Edges = 4 edges r=4: [Edge31,Edge37,Edge43,Edge46]
FEATURE [Part::Cut] Cut034
  Base = -> Chamfer011
  Placement = pos=(-5,40,3) rot=(1,0,0;3.14159rad)
  Tool = -> Fusion038
FEATURE [Part::Cut] Cut033
  Base = -> Cut034
  Placement = pos=(40,40,0) rot=(0,0,1;3.14159rad)
  Tool = -> Box124
FEATURE [Part::Sphere] Sphere047
  Angle1 = -90
  Angle2 = 90
  Angle3 = 360
  AttacherType = Attacher::AttachEngine3D
  Placement = pos=(-3,11.5,2.5) rot=(0,0,1;0rad)
  Radius = 1.25
FEATURE [Part::Box] Box132  label="Cube116"
  AttacherType = Attacher::AttachEngine3D
  Height = 7
  Length = 10
  Placement = pos=(-10,6,0) rot=(0,0,1;0rad)
  Width = 2
FEATURE [Part::Box] Box133  label="Cube117"
  AttacherType = Attacher::AttachEngine3D
  Height = 7
  Length = 4
  Placement = pos=(-1,8,0) rot=(0,0,1;0rad)
  Width = 2
FEATURE [Part::Box] Box134  label="Cube118"
  AttacherType = Attacher::AttachEngine3D
  Height = 7
  Length = 10
  Placement = pos=(-10,10,0) rot=(0,0,1;0rad)
  Width = 2
FEATURE [Part::Box] Box135  label="Cube119"
  AttacherType = Attacher::AttachEngine3D
  Height = 10
  Length = 12
  Placement = pos=(-11,-2,-12) rot=(0,0,1;0rad)
  Width = 44
FEATURE [Part::Box] Box136  label="Cube120"
  AttacherType = Attacher::AttachEngine3D
  Height = 7
  Length = 4
  Placement = pos=(-1,5,0) rot=(0,0,1;0rad)
  Width = 1
FEATURE [Part::Sphere] Sphere048
  Angle1 = -90
  Angle2 = 90
  Angle3 = 360
  AttacherType = Attacher::AttachEngine3D
  Placement = pos=(-3,28,2.5) rot=(0,0,1;0rad)
  Radius = 1.5
FEATURE [Part::Sphere] Sphere049
  Angle1 = -90
  Angle2 = 90
  Angle3 = 360
  AttacherType = Attacher::AttachEngine3D
  Placement = pos=(-3,6.5,2.5) rot=(0,0,1;0rad)
  Radius = 1.25
FEATURE [Part::Sphere] Sphere050
  Angle1 = -90
  Angle2 = 90
  Angle3 = 360
  AttacherType = Attacher::AttachEngine3D
  Placement = pos=(-3,34,2.5) rot=(0,0,1;0rad)
  Radius = 1.5
FEATURE [Part::Box] Box137  label="Cube121"
  AttacherType = Attacher::AttachEngine3D
  Height = 7
  Length = 4
  Placement = pos=(-1,12,0) rot=(0,0,1;0rad)
  Width = 1
FEATURE [Part::Box] Box138  label="Cube122"
  AttacherType = Attacher::AttachEngine3D
  Height = 7
  Length = 5
  Width = 40
FEATURE [Part::Box] Box139  label="Cube123"
  AttacherType = Attacher::AttachEngine3D
  Height = 7
  Length = 4
  Placement = pos=(-1,36.6,0) rot=(0,0,1;0rad)
  Width = 1
FEATURE [Part::Box] Box140  label="Cube124"
  AttacherType = Attacher::AttachEngine3D
  Height = 7
  Length = 4
  Placement = pos=(-1,24.4,0) rot=(0,0,1;0rad)
  Width = 1
FEATURE [Part::Box] Box141  label="Cube125"
  AttacherType = Attacher::AttachEngine3D
  Height = 7
  Length = 10
  Placement = pos=(-10,25.4,0) rot=(0,0,1;0rad)
  Width = 2
FEATURE [Part::Box] Box142  label="Cube126"
  AttacherType = Attacher::AttachEngine3D
  Height = 10
  Length = 13
  Placement = pos=(-10.19,0,-1.19) rot=(0,-1,0;0.785398rad)
  Width = 40
FEATURE [Part::Box] Box143  label="Cube127"
  AttacherType = Attacher::AttachEngine3D
  Height = 7
  Length = 10
  Placement = pos=(-10,34.6,0) rot=(0,0,1;0rad)
  Width = 2
FEATURE [Part::MultiFuse] Fusion044
  Shapes = -> [Box138,Box132,Box134,Box141,Box143]
FEATURE [Part::Cut] Cut037
  Base = -> Fusion044
  Tool = -> Box142
FEATURE [Part::MultiFuse] Fusion042
  Shapes = -> [Sphere049,Sphere047,Cut037]
FEATURE [Part::MultiFuse] Fusion045
  Shapes = -> [Sphere050,Sphere048]
FEATURE [Part::Cut] Cut038
  Base = -> Fusion042
  Tool = -> Fusion045
FEATURE [Part::Chamfer] Chamfer012
  Base = -> Cut038
  Edges = 4 edges r=4: [Edge31,Edge37,Edge43,Edge46]
FEATURE [Part::Box] Box144  label="Cube128"
  AttacherType = Attacher::AttachEngine3D
  Height = 7
  Length = 4
  Placement = pos=(-1,27.4,0) rot=(0,0,1;0rad)
  Width = 7.2
FEATURE [Part::MultiFuse] Fusion043
  Shapes = -> [Box144,Box137,Box139,Box133,Box140,Box136]
FEATURE [Part::Cut] Cut040
  Base = -> Chamfer012
  Placement = pos=(-5,40,3) rot=(1,0,0;3.14159rad)
  Tool = -> Fusion043
FEATURE [Part::Cut] Cut039
  Base = -> Cut040
  Placement = pos=(0,40,0) rot=(0,0,-1;1.5708rad)
  Tool = -> Box135
FEATURE [Part::MultiFuse] Fusion046
  Shapes = -> [Cut039,Cut028,Cut032,Cut033]
FEATURE [Part::MultiFuse] Fusion047
  Placement = pos=(0,40,6.7) rot=(1,0,0;3.14159rad)
  Shapes = -> [Fusion026,Fusion024,Fusion025]
FEATURE [Part::MultiFuse] Fusion048
  Shapes = -> [Box089,Box091,Box090,Box092]
FEATURE [Part::Fuse] Fusion049
  Base = -> Box075
  Tool = -> Fusion046
FEATURE [Part::Cut] Cut041
  Base = -> Fusion049
  Tool = -> Fusion047
FEATURE [Part::Cut] Cut042
  Base = -> Cut041
  Tool = -> Fusion048
FEATURE [Part::Box] Box145  label="Cube129"
  AttacherType = Attacher::AttachEngine3D
  Height = 15
  Length = 16
  Placement = pos=(12,12,-13) rot=(0,0,1;0rad)
  Width = 16
FEATURE [Part::Box] Box146  label="Cube130"
  AttacherType = Attacher::AttachEngine3D
  Height = 15
  Length = 16.5
  Placement = pos=(11.75,11.75,-3) rot=(0,0,1;0rad)
  Width = 16.5
FEATURE [Part::Chamfer] Chamfer013
  Base = -> Box146
  Edges = 4 edges r=4: [Edge1,Edge3,Edge5,Edge7]
FEATURE [Part::Box] Box147  label="Cube131"
  AttacherType = Attacher::AttachEngine3D
  Height = 10
  Length = 21
  Placement = pos=(9.5,9.5,2.1) rot=(0,0,1;0rad)
  Width = 21
FEATURE [Part::Box] Box148  label="Cube132"
  AttacherType = Attacher::AttachEngine3D
  Height = 14
  Length = 17
  Placement = pos=(11.5,11.5,0) rot=(0,0,1;0rad)
  Width = 17
FEATURE [Part::Cut] Cut043
  Base = -> Box147
  Tool = -> Box148
FEATURE [Part::Chamfer] Chamfer014
  Base = -> Cut043
  Edges = 8 edges r=0.95: [Edge4,Edge5,Edge14,Edge16,Edge17,Edge18,Edge19,Edge20]
FEATURE [Part::Cut] Cut044
  Base = -> Cut042
  Tool = -> Chamfer014
FEATURE [Part::Cut] Cut045
  Base = -> Cut044
  Tool = -> Chamfer013
FEATURE [Part::Cut] Cut046
  Base = -> Cut045
  Tool = -> Box145
